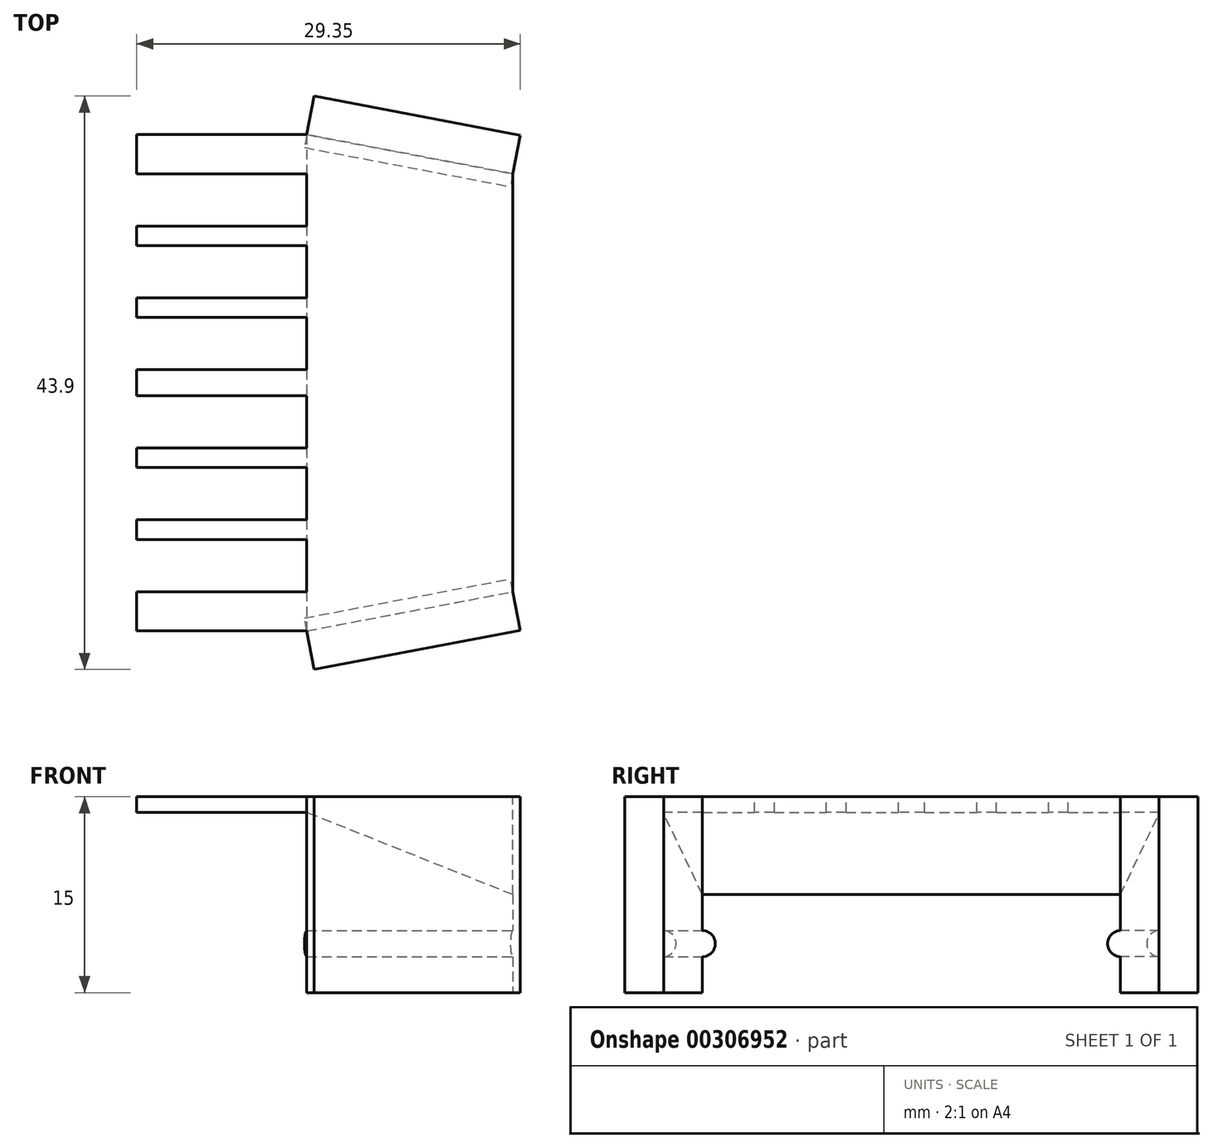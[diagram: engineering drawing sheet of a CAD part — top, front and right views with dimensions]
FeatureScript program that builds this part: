
annotation { "Feature Type Name" : "Feature", "Feature Type Description" : "" }
export const myFeature = defineFeature(function(context is Context, id is Id, definition is map)
    precondition{}
    {
        {
            var Q0;
            Q0=qCreatedBy(makeId("Front.planeOp"),FACE);
            var sketch = newSketch(context, id + "F0", { "sketchPlane" : qUnion([Q0])});
            skLineSegment(sketch, "E0.bottom", {"start": v(-13, 0) * mm, "end": v(0, 0) * mm});
            skLineSegment(sketch, "E0.top", {"start": v(-13, 1.2) * mm, "end": v(15.79, 1.2) * mm});
            skLineSegment(sketch, "E0.left", {"start": v(-13, 0) * mm, "end": v(-13, 1.2) * mm});
            skLineSegment(sketch, "E1", {"start": v(0, 0) * mm, "end": v(15.79, -6.3) * mm});
            skLineSegment(sketch, "E2", {"start": v(15.79, -6.3) * mm, "end": v(15.79, 1.2) * mm});
            skSolve(sketch);
        }
        {
            var Q0;
            Q0=makeQuery(id+"F0.imprint","IMPRINT",FACE,{"disambiguationData":[TD([[makeQuery(id+"F0.imprint","IMPRINT",EDGE,{"derivedFrom":sQuery(id+"F0.wireOp",EDGE,"E0.bottom")}),1.0]])]});
            extrude(context, id + "F1", {"entities" : qUnion([Q0]), "oppositeDirection" : true, "depth" : 38 * mm});
        }
        {
            var Q0;
            Q0=makeQuery(id+"F1.opExtrude","SWEPT_FACE",FACE,{"disambiguationData":[OSD([sQuery(id+"F0.wireOp",EDGE,"E0.top")])]});
            var sketch = newSketch(context, id + "F2", { "sketchPlane" : qUnion([Q0])});
            skLineSegment(sketch, "E3.bottom", {"start": v(-13, 35) * mm, "end": v(0, 35) * mm});
            skLineSegment(sketch, "E3.top", {"start": v(-13, 31) * mm, "end": v(0, 31) * mm});
            skLineSegment(sketch, "E3.left", {"start": v(-13, 35) * mm, "end": v(-13, 31) * mm});
            skLineSegment(sketch, "E3.right", {"start": v(0, 35) * mm, "end": v(0, 31) * mm});
            skLineSegment(sketch, "E4.bottom", {"start": v(0, 29.5) * mm, "end": v(-13, 29.5) * mm});
            skLineSegment(sketch, "E4.top", {"start": v(0, 25.5) * mm, "end": v(-13, 25.5) * mm});
            skLineSegment(sketch, "E4.left", {"start": v(0, 29.5) * mm, "end": v(0, 25.5) * mm});
            skLineSegment(sketch, "E4.right", {"start": v(-13, 29.5) * mm, "end": v(-13, 25.5) * mm});
            skLineSegment(sketch, "E5.left", {"start": v(0, 24) * mm, "end": v(0, 20) * mm});
            skLineSegment(sketch, "E6.bottom", {"start": v(0, 18) * mm, "end": v(-13, 18) * mm});
            skLineSegment(sketch, "E6.top", {"start": v(0, 14) * mm, "end": v(-13, 14) * mm});
            skLineSegment(sketch, "E6.left", {"start": v(0, 18) * mm, "end": v(0, 14) * mm});
            skLineSegment(sketch, "E6.right", {"start": v(-13, 18) * mm, "end": v(-13, 14) * mm});
            skLineSegment(sketch, "E7.bottom", {"start": v(0, 12.5) * mm, "end": v(-13, 12.5) * mm});
            skLineSegment(sketch, "E7.top", {"start": v(0, 8.5) * mm, "end": v(-13, 8.5) * mm});
            skLineSegment(sketch, "E7.left", {"start": v(0, 12.5) * mm, "end": v(0, 8.5) * mm});
            skLineSegment(sketch, "E7.right", {"start": v(-13, 12.5) * mm, "end": v(-13, 8.5) * mm});
            skLineSegment(sketch, "E8.bottom", {"start": v(0, 7) * mm, "end": v(-13, 7) * mm});
            skLineSegment(sketch, "E8.top", {"start": v(0, 3) * mm, "end": v(-13, 3) * mm});
            skLineSegment(sketch, "E8.left", {"start": v(0, 7) * mm, "end": v(0, 3) * mm});
            skLineSegment(sketch, "E8.right", {"start": v(-13, 7) * mm, "end": v(-13, 3) * mm});
            skLineSegment(sketch, "E9", {"start": v(0, 24) * mm, "end": v(-13, 24) * mm});
            skLineSegment(sketch, "E10", {"start": v(0, 20) * mm, "end": v(-13, 20) * mm});
            skLineSegment(sketch, "E11", {"start": v(-13, 20) * mm, "end": v(-13, 24) * mm});
            skLineSegment(sketch, "E12", {"start": v(0, 0) * mm, "end": v(15.79, 3) * mm});
            skLineSegment(sketch, "E13", {"start": v(0, 38) * mm, "end": v(15.79, 35) * mm});
            skLineSegment(sketch, "E14", {"start": v(0, 0) * mm, "end": v(15.79, 0) * mm});
            skLineSegment(sketch, "E15", {"start": v(15.79, 0) * mm, "end": v(15.79, 3) * mm});
            skLineSegment(sketch, "E16", {"start": v(15.79, 35) * mm, "end": v(15.79, 38) * mm});
            skLineSegment(sketch, "E17", {"start": v(0, 38) * mm, "end": v(15.79, 38) * mm});
            skSolve(sketch);
        }
        {
            var Q0;
            Q0 = qSketchRegion(id + "F2", true);
            extrude(context, id + "F3", {"entities" : qUnion([Q0]), "operationType" : NewBodyOperationType.REMOVE, "endBound" : BoundingType.THROUGH_ALL, "oppositeDirection" : true, "depth" : 25 * mm});
        }
        {
            var Q0;
            Q0=makeQuery(id+"F3.boolean.opBoolean","COPY",FACE,{"derivedFrom":makeQuery(id+"F3.opExtrude","SWEPT_FACE",FACE,{"disambiguationData":[OSD([sQuery(id+"F2.wireOp",EDGE,"E13")])]})});
            var sketch = newSketch(context, id + "F4", { "sketchPlane" : qUnion([Q0])});
            skLineSegment(sketch, "E18.bottom", {"start": v(-8.98, 1.2) * mm, "end": v(7.1, 1.2) * mm});
            skLineSegment(sketch, "E18.top", {"start": v(-8.98, -13.8) * mm, "end": v(7.1, -13.8) * mm});
            skLineSegment(sketch, "E18.left", {"start": v(-8.98, 1.2) * mm, "end": v(-8.98, -13.8) * mm});
            skLineSegment(sketch, "E18.right", {"start": v(7.1, 1.2) * mm, "end": v(7.1, -13.8) * mm});
            skSolve(sketch);
        }
        {
            var Q0;
            Q0 = qSketchRegion(id + "F4", true);
            extrude(context, id + "F5", {"entities" : qUnion([Q0]), "operationType" : NewBodyOperationType.ADD, "depth" : 3 * mm});
        }
        {
            var Q0;
            Q0=makeQuery(id+"F3.boolean.opBoolean","COPY",FACE,{"derivedFrom":makeQuery(id+"F3.opExtrude","SWEPT_FACE",FACE,{"disambiguationData":[OSD([sQuery(id+"F2.wireOp",EDGE,"E12")])]})});
            var sketch = newSketch(context, id + "F6", { "sketchPlane" : qUnion([Q0])});
            skLineSegment(sketch, "E19.bottom", {"start": v(0, 1.2) * mm, "end": v(16.07, 1.2) * mm});
            skLineSegment(sketch, "E19.top", {"start": v(0, -13.8) * mm, "end": v(16.07, -13.8) * mm});
            skLineSegment(sketch, "E19.left", {"start": v(0, 1.2) * mm, "end": v(0, -13.8) * mm});
            skLineSegment(sketch, "E19.right", {"start": v(16.07, 1.2) * mm, "end": v(16.07, -13.8) * mm});
            skSolve(sketch);
        }
        {
            var Q0;
            {var subQ0=sQuery(id+"F6.wireOp",EDGE,"E19.top");Q0=makeQuery(id+"F6.imprint","IMPRINT",FACE,{"disambiguationData":[TD([[makeQuery(id+"F6.imprint","IMPRINT",EDGE,{"derivedFrom":subQ0}),1.0]])]});}
            var Q1;
            Q1 = qSketchRegion(id + "F6", true);
            extrude(context, id + "F7", {"entities" : qUnion([Q0, Q1]), "operationType" : NewBodyOperationType.ADD, "depth" : 3 * mm});
        }
        {
            var Q0;
            Q0=makeQuery(id+"F5.opExtrude","SWEPT_FACE",FACE,{"disambiguationData":[OSD([sQuery(id+"F4.wireOp",EDGE,"E18.left")])]});
            var sketch = newSketch(context, id + "F8", { "sketchPlane" : qUnion([Q0])});
            skArc(sketch, "E20", {"start": v(37.33, -9.05) * mm, "mid": v(36.33, -10.05) * mm, "end": v(37.33, -11.05) * mm});
            skLineSegment(sketch, "E21", {"start": v(37.33, -11.05) * mm, "end": v(37.33, -9.05) * mm});
            skSolve(sketch);
        }
        {
            var Q0;
            Q0 = qSketchRegion(id + "F8", true);
            extrude(context, id + "F9", {"entities" : qUnion([Q0]), "operationType" : NewBodyOperationType.ADD, "oppositeDirection" : true, "depth" : 16.05 * mm});
        }
        {
            var Q0;
            Q0=makeQuery(id+"F7.opExtrude","SWEPT_FACE",FACE,{"disambiguationData":[OSD([sQuery(id+"F6.wireOp",EDGE,"E19.right")])]});
            var sketch = newSketch(context, id + "F10", { "sketchPlane" : qUnion([Q0])});
            skArc(sketch, "E22", {"start": v(0, -11.05) * mm, "mid": v(1, -10.05) * mm, "end": v(0, -9.05) * mm});
            skLineSegment(sketch, "E23", {"start": v(0, -11.05) * mm, "end": v(0, -9.05) * mm});
            skSolve(sketch);
        }
        {
            var Q0;
            Q0 = qSketchRegion(id + "F10", true);
            extrude(context, id + "F11", {"entities" : qUnion([Q0]), "operationType" : NewBodyOperationType.ADD, "oppositeDirection" : true, "depth" : 16.05 * mm});
        }
    });
